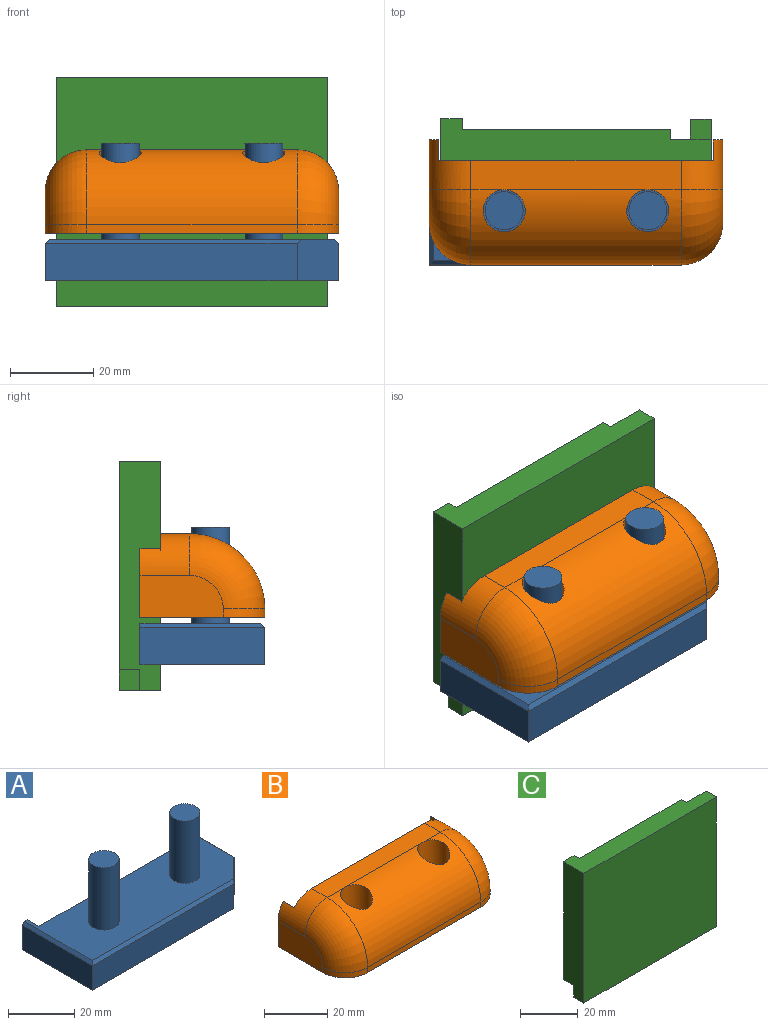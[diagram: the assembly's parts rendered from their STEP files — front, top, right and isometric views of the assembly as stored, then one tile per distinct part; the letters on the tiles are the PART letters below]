
ASSEMBLY  parts=3 mates=2
PART A: 18 faces, bbox 70.5x30x33 mm
  f0: cylinder r=4.55mm len=23mm, axis (0,0,-1), area 657.5mm2, adj f1,f5
  f1: plane 9.1x9.1mm, normal (0,0,1), area 65mm2, adj f0
  f2: plane 66.1x10mm, normal (0,1,0), area 661mm2, adj f5,f7,f9,f16
  f3: plane 30x9mm, normal (-1,0,0), area 270mm2, adj f6,f8,f12,f16
  f4: plane 20x9mm, normal (1,0,0), area 180mm2, adj f10,f13,f16,f17
  f5: plane 68.5x29mm, normal (0,0,1), area 1493.9mm2, adj f0,f2,f7,f8,f9,f10,f11,f12
  f6: plane 60.5x9mm, normal (0,-1,0), area 544.5mm2, adj f3,f11,f16,f17
  f7: plane 10x5mm, normal (1,0,0), area 50mm2, adj f2,f5,f8,f16
  f8: plane 10x2.2mm, normal (0,1,0), area 21.5mm2, adj f3,f5,f7,f12,f16
  f9: plane 10x5mm, normal (-1,0,0), area 50mm2, adj f2,f5,f10,f16
  f10: plane 10x2.2mm, normal (0,1,0), area 21.5mm2, adj f4,f5,f9,f13,f16
  f11: plane 61.5x1mm, normal (0,-0.71,0.71), area 85.6mm2, adj f5,f6,f12,f17
  f12: plane 30x1mm, normal (-0.71,0,0.71), area 41.7mm2, adj f3,f5,f8,f11
  f13: plane 21x1mm, normal (0.71,0,0.71), area 29mm2, adj f4,f5,f10,f17
  f14: cylinder r=4.55mm len=23mm, axis (0,0,-1), area 657.5mm2, adj f5,f15
  f15: plane 9.1x9.1mm, normal (0,0,1), area 65mm2, adj f14
  f16: plane 70.5x30mm, normal (0,0,-1), area 1734.5mm2, adj f2,f3,f4,f6,f7,f8,f9,f10
  f17: plane 10x10mm, normal (0.71,-0.71,0), area 140mm2, adj f4,f5,f6,f11,f13,f16
PART B: 19 faces, bbox 70.5x30x20 mm
  f0: plane 65.9x20mm, normal (0,1,0), area 1301mm2, adj f2,f4,f6,f8,f15,f16
  f1: plane 20x10mm, normal (-1,0,0), area 186.3mm2, adj f2,f7,f16,f17,f18
  f2: plane 70.5x30mm, normal (0,0,-1), area 1582.3mm2, adj f0,f1,f3,f5,f6,f7,f8,f9
  f3: plane 20x10mm, normal (1,0,0), area 186.3mm2, adj f2,f9,f13,f14,f15
  f4: plane 50.5x7mm, normal (0,0,1), area 353.4mm2, adj f0,f10,f11,f12,f15,f16
  f5: plane 50.5x2mm, normal (0,-1,0), area 101mm2, adj f2,f12,f13,f18
  f6: plane 16.38x5mm, normal (1,0,0), area 81.9mm2, adj f0,f2,f7,f16
  f7: plane 16.38x2.3mm, normal (0,1,0), area 33mm2, adj f1,f2,f6,f16
  f8: plane 16.38x5mm, normal (-1,0,0), area 81.9mm2, adj f0,f2,f9,f15
  f9: plane 16.38x2.3mm, normal (0,1,0), area 33mm2, adj f2,f3,f8,f15
  f10: cylinder r=5.05mm len=20mm, axis (0,0,-1), area 599.2mm2, adj f2,f4,f12
  f11: cylinder r=5.05mm len=20mm, axis (0,0,-1), area 599.2mm2, adj f2,f4,f12
  f12: cylinder r=18mm len=50.5mm, axis (1,0,0), area 1258.7mm2, adj f4,f5,f10,f11,f14,f17
  f13: cylinder r=10mm len=10mm, axis (0,0,-1), area 31.4mm2, adj f2,f3,f5,f14
  f14: torus R=8mm, axis (1,0,0), area 354.5mm2, adj f3,f12,f13,f15
  f15: cylinder r=10mm len=12mm, axis (0,1,0), area 144.6mm2, adj f0,f3,f4,f8,f9,f14
  f16: cylinder r=10mm len=12mm, axis (0,-1,0), area 144.6mm2, adj f0,f1,f4,f6,f7,f17
  f17: torus R=8mm, axis (1,0,0), area 354.5mm2, adj f1,f12,f16,f18
  f18: cylinder r=10mm len=10mm, axis (0,0,1), area 31.4mm2, adj f1,f2,f5,f17
PART C: 15 faces, bbox 65x10x55 mm
  f0: plane 65x55mm, normal (0,1,0), area 3040.3mm2, adj f1,f2,f3,f4,f6,f7,f9,f11
  f1: plane 55x10mm, normal (-1,0,0), area 525mm2, adj f0,f2,f4,f5,f9,f10
  f2: plane 65x10mm, normal (0,0,-1), area 350mm2, adj f0,f1,f3,f5,f13,f14
  f3: plane 55x10mm, normal (1,0,0), area 299.8mm2, adj f0,f2,f4,f5,f12,f14
  f4: plane 65x10mm, normal (0,0,1), area 476mm2, adj f0,f1,f3,f5,f7,f8,f10,f11
  f5: plane 65x55mm, normal (0,-1,0), area 3575mm2, adj f1,f2,f3,f4
  f6: plane 50x2.5mm, normal (0,0,-1), area 125mm2, adj f0,f7,f8,f11
  f7: plane 5x2.5mm, normal (1,0,0), area 12.5mm2, adj f0,f4,f6,f8
  f8: plane 50x5mm, normal (0,1,0), area 250mm2, adj f4,f6,f7,f11
  f9: plane 5.2x5mm, normal (0,0,-1), area 26mm2, adj f0,f1,f10,f11
  f10: plane 50x5.2mm, normal (0,1,0), area 260mm2, adj f1,f4,f9,f11
  f11: plane 50x5mm, normal (1,0,0), area 237.5mm2, adj f0,f4,f6,f8,f9,f10
  f12: plane 5x5mm, normal (0,0,1), area 25mm2, adj f0,f3,f13,f14
  f13: plane 5x4.95mm, normal (-1,0,0), area 24.8mm2, adj f0,f2,f12,f14
  f14: plane 5x4.95mm, normal (0,1,0), area 24.8mm2, adj f2,f3,f12,f13
PLACE A t=(50.92,-21.48,1.34)mm
PLACE B t=(-23.58,-21.48,13.28)mm
PLACE C t=(-22.89,-16.48,50.26)mm
MATE fastened A.f0 <-> B.f11  axis (0,0,-1) through (26.86,-33.48,22.94)mm
MATE fastened C.f5 <-> B.f0  axis (0,-1,0) through (9.61,-21.48,22.76)mm
